FCSTD DOCUMENT  (FreeCAD 0.21R33668 +26 (Git))
Label: eurorack_adapter_assy
License: All rights reserved
LicenseURL: https://en.wikipedia.org/wiki/All_rights_reserved
objects: Part::FeaturePython×2, App::FeaturePython×2, Sketcher::SketchObject×1, PartDesign::Body×1
note: 4 computed .brp shape members not serialized (recipe doc carries the construction recipe); baked Part::Feature solids carry a one-line shape summary decoded from their .brp

FEATURE [Part::FeaturePython] b_assembly_main_001_  label="assembly_main_001"  # a2plus imported part (geometry in sourceFile) (typed FeaturePython)
  a2p_Version = 0.4.61
  fixedPosition = true
  objectType = a2pPart
  sourceFile = .\..\..\Design\Assembly\assembly_main.FCStd
  subassemblyImport = true
  timeLastImport = 1.70428e+09
  updateColors = true
FEATURE [Part::FeaturePython] b_eurorack_adapter_001_  label="eurorack_adapter_001"  # a2plus imported part (geometry in sourceFile) (typed FeaturePython)
  Placement = pos=(-0.269056,0.231112,1.4) rot=(0,0,-1;4.71235rad)
  a2p_Version = 0.4.61
  fixedPosition = false
  objectType = a2pPart
  sourceFile = .\..\Eurorack_adapter\eurorack_adapter.FCStd
  subassemblyImport = false
  timeLastImport = 1.70498e+09
  updateColors = true
FEATURE [Sketcher::SketchObject] Sketch
  FullyConstrained = true
  MapMode = 5
  Placement = pos=(0,0,0) rot=(0.57735,0.57735,0.57735;2.0944rad)
  Support = -> [YZ_Plane]
FEATURE [PartDesign::Body] Body
  Group = -> [Sketch]
  Origin = -> Origin
FEATURE [App::FeaturePython] planeCoincident_001  label="planeCoincident_001__assembly_main_001"  # a2plus constraint (typed FeaturePython)
  Object1 = b_eurorack_adapter_001_
  Object2 = b_assembly_main_001_
  ParentTreeObject = -> b_eurorack_adapter_001_
  SubElement1 = Face146
  SubElement2 = Face81
  Suppressed = false
  Type = plane
  directionConstraint = 0
  offset = 0
FEATURE [App::FeaturePython] planeCoincident_001_mirror  label="planeCoincident_001__eurorack_adapter_001"  # a2plus constraint (typed FeaturePython)
  Object1 = b_eurorack_adapter_001_
  Object2 = b_assembly_main_001_
  ParentTreeObject = -> b_assembly_main_001_
  SubElement1 = Face146
  SubElement2 = Face81
  Suppressed = false
  Type = plane
  directionConstraint = 0
  offset = 0
